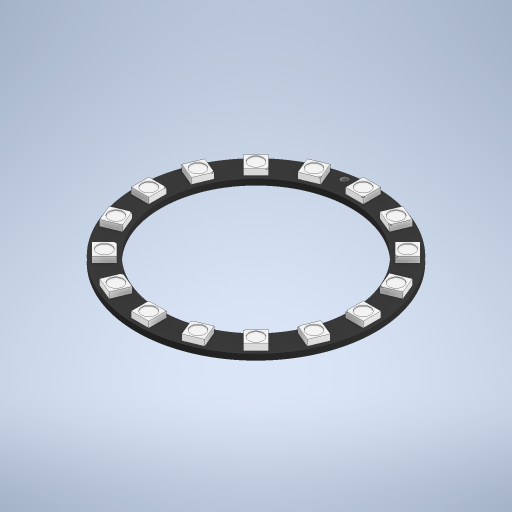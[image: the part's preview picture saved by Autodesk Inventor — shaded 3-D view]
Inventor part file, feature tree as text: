
AUTODESK INVENTOR PART (.ipt)
format: ipt  version: 2023 (Build 270158000, 158)  size: 433,664 bytes
history: native  units: mm
features: extrude x4, sketch x3, other x1, pattern_circular x1, projected_geometry x1
ambient origin geometry x8: Origin, YZ Plane, XZ Plane, XY Plane, X Axis, Y Axis, Z Axis, Center Point
bodies: Body1 (feature_tree)
feature tree (10):
  other  "솔리드1"
  sketch  "스케치2"
  extrude  "돌출1"  Depth=68.0mm
  extrude  "돌출2"  Depth=54.0mm
  extrude  "돌출3"  Depth=5.0mm
  pattern_circular  "원형 패턴1"  [2 undecoded]
  extrude  "돌출4"  Depth=33.0mm
  sketch  "스케치3"
  projected_geometry  "투영된 루프1"
  sketch  "스케치4"
note: 2 required parameter values undecoded (feature->parameter linkage not recoverable at this tier; creation-order binding heuristic only, values carry confidence <= 0.55)
